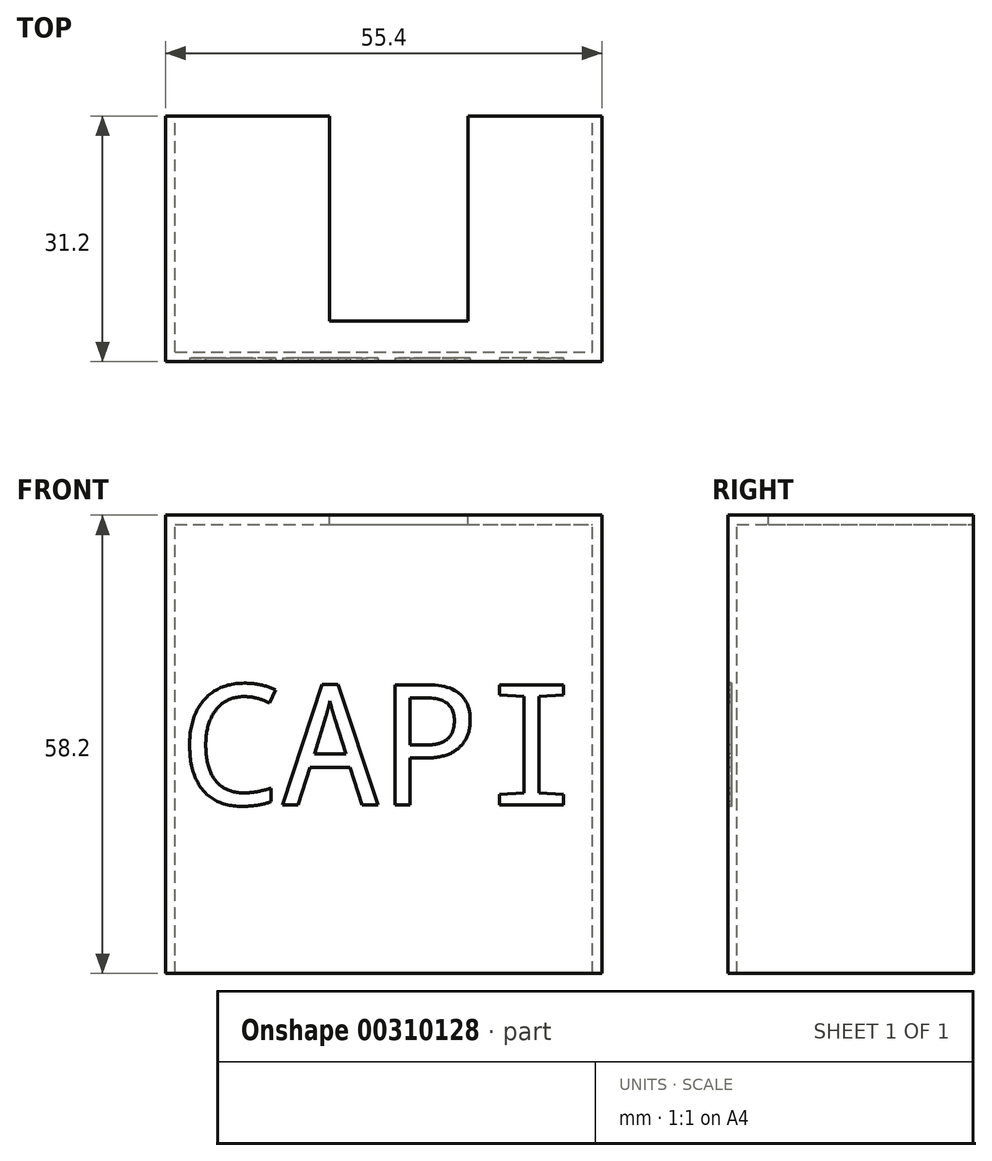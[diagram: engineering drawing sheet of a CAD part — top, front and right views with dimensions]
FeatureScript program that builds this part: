
annotation { "Feature Type Name" : "Feature", "Feature Type Description" : "" }
export const myFeature = defineFeature(function(context is Context, id is Id, definition is map)
    precondition{}
    {
        {
            assignVariable(context, id + "F0", {"name" : "wallth", "anyValue" : 1.2});
        }
        {
            var Q0;
            Q0=qCreatedBy(makeId("Top.planeOp"),FACE);
            var sketch = newSketch(context, id + "F1", { "sketchPlane" : qUnion([Q0])});
            skLineSegment(sketch, "E0.bottom", {"start": v(0, 0) * mm, "end": v(55.4, 0) * mm});
            skLineSegment(sketch, "E0.top", {"start": v(0, 31.2) * mm, "end": v(55.4, 31.2) * mm});
            skLineSegment(sketch, "E0.left", {"start": v(0, 0) * mm, "end": v(0, 31.2) * mm});
            skLineSegment(sketch, "E0.right", {"start": v(55.4, 0) * mm, "end": v(55.4, 31.2) * mm});
            skSolve(sketch);
        }
        {
            var Q0;
            Q0=makeQuery(id+"F1.imprint","IMPRINT",FACE,{"disambiguationData":[TD([[makeQuery(id+"F1.imprint","IMPRINT",EDGE,{"derivedFrom":sQuery(id+"F1.wireOp",EDGE,"E0.bottom")}),1.0]])]});
            extrude(context, id + "F2", {"entities" : qUnion([Q0]), "oppositeDirection" : true, "depth" : (57 + getVariable(context, 'wallth')) * mm});
        }
        {
            var Q0;
            Q0=makeQuery(id+"F2.opExtrude","SWEPT_FACE",FACE,{"disambiguationData":[OSD([sQuery(id+"F1.wireOp",EDGE,"E0.top")])]});
            var Q1;
            Q1=makeQuery(id+"F2.opExtrude","CAP_FACE",FACE,{"disambiguationData":[OSD([sQuery(id+"F1.wireOp",EDGE,"E0.bottom"),sQuery(id+"F1.wireOp",EDGE,"E0.top"),sQuery(id+"F1.wireOp",EDGE,"E0.left"),sQuery(id+"F1.wireOp",EDGE,"E0.right")])],"isStart":false});
            shell(context, id + "F3", {"entities" : qUnion([Q0, Q1]), "thickness" : (getVariable(context, 'wallth')) * mm});
        }
        {
            var Q0;
            Q0=makeQuery(id+"F2.opExtrude","CAP_FACE",FACE,{"disambiguationData":[OSD([sQuery(id+"F1.wireOp",EDGE,"E0.bottom"),sQuery(id+"F1.wireOp",EDGE,"E0.top"),sQuery(id+"F1.wireOp",EDGE,"E0.left"),sQuery(id+"F1.wireOp",EDGE,"E0.right")])],"isStart":true});
            var sketch = newSketch(context, id + "F4", { "sketchPlane" : qUnion([Q0])});
            skLineSegment(sketch, "E1.bottom", {"start": v(38.4, 31.2) * mm, "end": v(20.8, 31.2) * mm});
            skLineSegment(sketch, "E1.top", {"start": v(38.4, 5.2) * mm, "end": v(20.8, 5.2) * mm});
            skLineSegment(sketch, "E1.left", {"start": v(38.4, 31.2) * mm, "end": v(38.4, 5.2) * mm});
            skLineSegment(sketch, "E1.right", {"start": v(20.8, 31.2) * mm, "end": v(20.8, 5.2) * mm});
            skSolve(sketch);
        }
        {
            var Q0;
            Q0=makeQuery(id+"F4.imprint","IMPRINT",FACE,{"disambiguationData":[TD([[makeQuery(id+"F4.imprint","IMPRINT",EDGE,{"derivedFrom":sQuery(id+"F4.wireOp",EDGE,"E1.bottom")}),-1.0]])]});
            var Q1;
            Q1=makeQuery(id+"F3.opShell","OFFSET_FACE",FACE,{"disambiguationData":[OSD([sQuery(id+"F1.wireOp",EDGE,"E0.bottom"),sQuery(id+"F1.wireOp",EDGE,"E0.top"),sQuery(id+"F1.wireOp",EDGE,"E0.left"),sQuery(id+"F1.wireOp",EDGE,"E0.right")])]});
            extrude(context, id + "F5", {"entities" : qUnion([Q0]), "operationType" : NewBodyOperationType.REMOVE, "endBound" : BoundingType.UP_TO_SURFACE, "oppositeDirection" : true, "endBoundEntityFace" : qUnion([Q1]), "depth" : 25 * mm});
        }
        {
            var Q0;
            Q0=makeQuery(id+"F2.opExtrude","SWEPT_FACE",FACE,{"disambiguationData":[OSD([sQuery(id+"F1.wireOp",EDGE,"E0.bottom")])]});
            var sketch = newSketch(context, id + "F6", { "sketchPlane" : qUnion([Q0])});
            skText(sketch, "E2", { "text": "CAPI", "fontName": "DroidSansMono.ttf"});
            skLineSegment(sketch, "E3", {"start": v(27.7, 0) * mm, "end": v(27.7, -58.2) * mm, "construction": true});
            skLineSegment(sketch, "E4", {"start": v(0, -29.1) * mm, "end": v(55.4, -29.1) * mm, "construction": true});
            const initialGuessF6  = {"E2": [0.0017, -0.03677, 1, 0, 0.01535]};
            skSetInitialGuess(sketch, initialGuessF6);
            skSolve(sketch);
        }
        {
            var Q0;
            Q0=makeQuery(id+"F6.imprint","IMPRINT",FACE,{"disambiguationData":[TD([[makeQuery(id+"F6.imprint","IMPRINT",EDGE,{"derivedFrom":sQuery(id+"F6.wireOp",EDGE,"E2.sketch_text.stroke-0")}),-1.0]])]});
            var Q1;
            Q1=makeQuery(id+"F6.imprint","IMPRINT",FACE,{"disambiguationData":[TD([[makeQuery(id+"F6.imprint","IMPRINT",EDGE,{"derivedFrom":sQuery(id+"F6.wireOp",EDGE,"E2.sketch_text.stroke-14")}),-1.0]])]});
            var Q2;
            Q2=makeQuery(id+"F6.imprint","IMPRINT",FACE,{"disambiguationData":[TD([[makeQuery(id+"F6.imprint","IMPRINT",EDGE,{"derivedFrom":sQuery(id+"F6.wireOp",EDGE,"E2.sketch_text.stroke-27")}),-1.0]])]});
            var Q3;
            Q3=makeQuery(id+"F6.imprint","IMPRINT",FACE,{"disambiguationData":[TD([[makeQuery(id+"F6.imprint","IMPRINT",EDGE,{"derivedFrom":sQuery(id+"F6.wireOp",EDGE,"E2.sketch_text.stroke-41")}),-1.0]])]});
            extrude(context, id + "F7", {"entities" : qUnion([Q0, Q1, Q2, Q3]), "operationType" : NewBodyOperationType.REMOVE, "oppositeDirection" : true, "depth" : 0.5 * mm});
        }
    });
